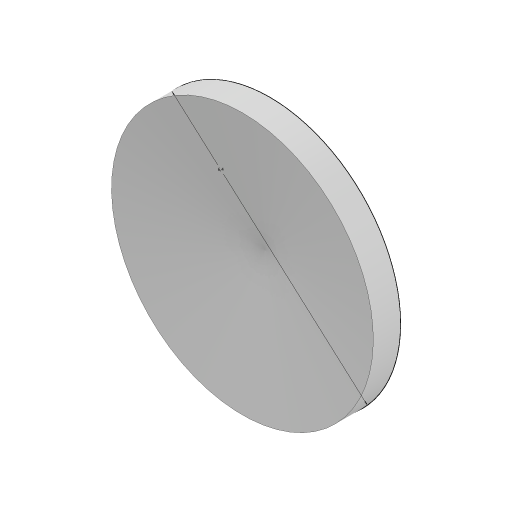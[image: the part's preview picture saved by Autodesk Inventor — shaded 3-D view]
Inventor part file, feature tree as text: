
AUTODESK INVENTOR PART (.ipt)
format: ipt  version: 2023.3 (Build 273359000, 359)  size: 106,496 bytes
history: native  units: mm
features: sketch x2, revolve x1
ambient origin geometry x8: Origin, YZ Plane, XZ Plane, XY Plane, X Axis, Y Axis, Z Axis, Center Point
bodies: Solid1 (feature_tree)
feature tree (3):
  sketch  "Sketch1"  dims[d0=6.4mm d1=3.2mm]
  revolve  "Revolution1"  [1 undecoded]
  sketch  "Sketch2"  dims[d3=0.1mm d4=1.745329mm d5=90.0deg]
note: 1 required parameter value undecoded (feature->parameter linkage not recoverable at this tier; creation-order binding heuristic only, values carry confidence <= 0.55)
